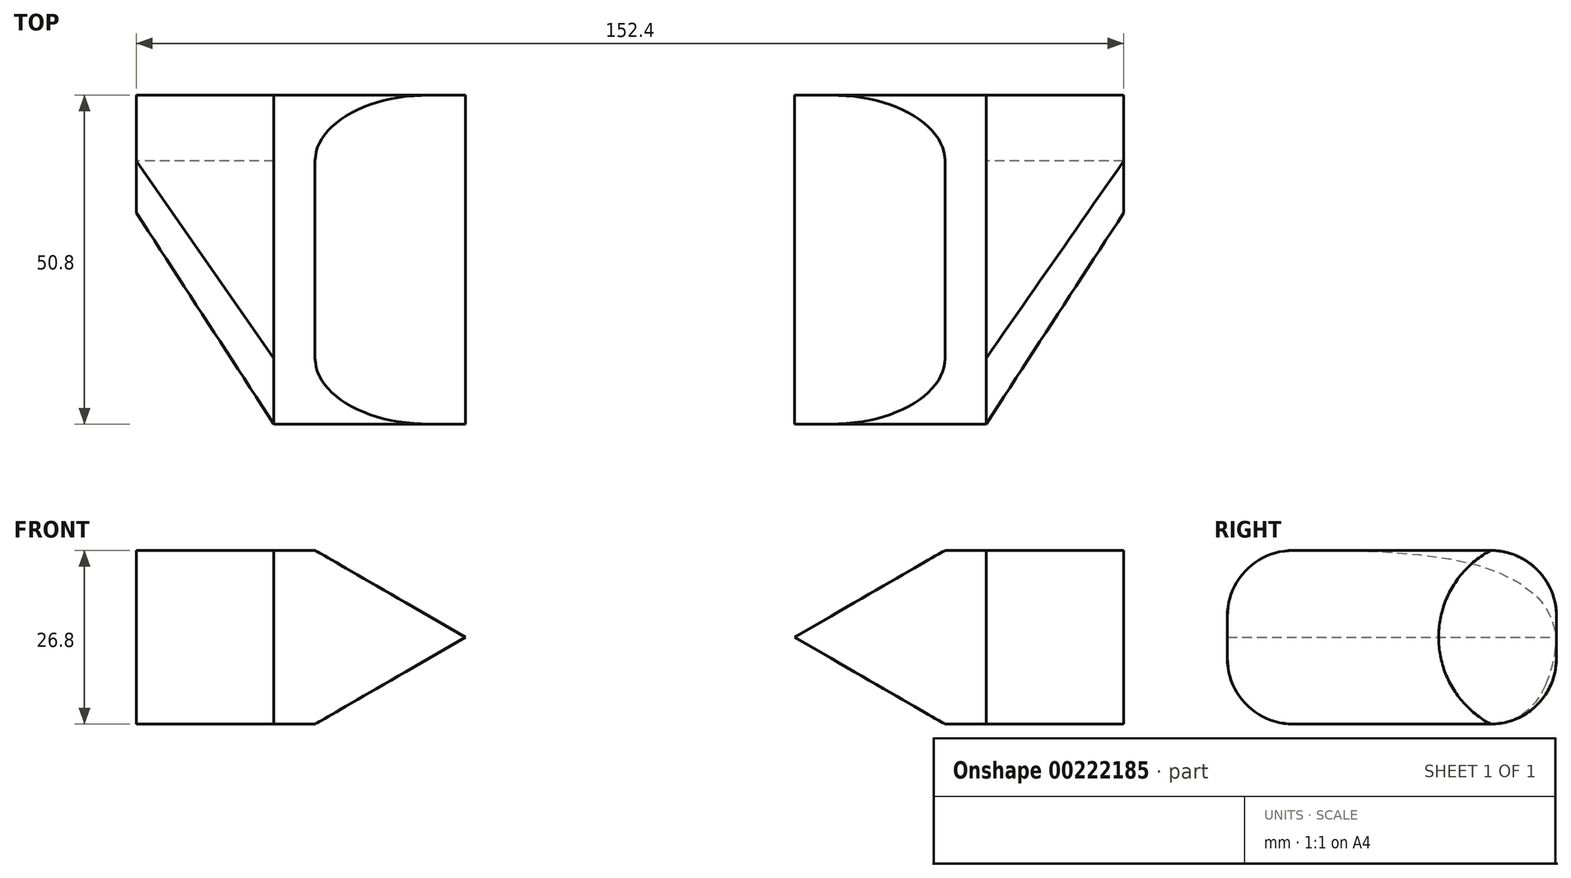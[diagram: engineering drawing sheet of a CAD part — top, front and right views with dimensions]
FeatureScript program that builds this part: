
annotation { "Feature Type Name" : "Feature", "Feature Type Description" : "" }
export const myFeature = defineFeature(function(context is Context, id is Id, definition is map)
    precondition{}
    {
        {
            var Q0;
            Q0=qCreatedBy(makeId("Front.planeOp"),FACE);
            var sketch = newSketch(context, id + "F0", { "sketchPlane" : qUnion([Q0])});
            skLineSegment(sketch, "E0", {"start": v(0, 47.56) * mm, "end": v(0, -56.2) * mm, "construction": true});
            skLineSegment(sketch, "E1", {"start": v(0, 0) * mm, "end": v(25.4, 0) * mm, "construction": true});
            skLineSegment(sketch, "E2.MirrorCS", {"start": v(0, 0) * mm, "end": v(-25.4, 0) * mm, "construction": true});
            skLineSegment(sketch, "E3", {"start": v(-25.4, 0) * mm, "end": v(-48.62, -13.4) * mm});
            skLineSegment(sketch, "E4", {"start": v(-48.62, -13.4) * mm, "end": v(-48.62, 13.4) * mm});
            skLineSegment(sketch, "E5", {"start": v(-48.62, 13.4) * mm, "end": v(-25.4, 0) * mm});
            skSolve(sketch);
        }
        {
            var Q0;
            Q0=makeQuery(id+"F0.imprint","IMPRINT",FACE,{"disambiguationData":[TD([[makeQuery(id+"F0.imprint","IMPRINT",EDGE,{"derivedFrom":sQuery(id+"F0.wireOp",EDGE,"E3")}),-1.0]])]});
            extrude(context, id + "F1", {"entities" : qUnion([Q0]), "depth" : 50.8 * mm});
        }
        {
            var Q0;
            Q0=makeQuery(id+"F1.opExtrude","SWEPT_FACE",FACE,{"disambiguationData":[OSD([sQuery(id+"F0.wireOp",EDGE,"E4")])]});
            extrude(context, id + "F2", {"entities" : qUnion([Q0]), "operationType" : NewBodyOperationType.ADD, "depth" : 6.35 * mm});
        }
        {
            var Q0;
            {var subQ0=sQuery(id+"F0.wireOp",EDGE,"E5");var subQ1=sQuery(id+"F0.wireOp",EDGE,"E4");Q0=makeQuery(id+"F2.opExtrude","SWEPT_EDGE",EDGE,{"disambiguationData":[OSD([subQ1,subQ0]),TDD([makeQuery(id+"F1.opExtrude","CAP_VERTEX",VERTEX,{"disambiguationData":[OSD([subQ1,subQ0])],"isStart":true})])]});}
            var Q1;
            {var subQ0=sQuery(id+"F0.wireOp",EDGE,"E4");var subQ1=sQuery(id+"F0.wireOp",EDGE,"E3");Q1=makeQuery(id+"F2.opExtrude","SWEPT_EDGE",EDGE,{"disambiguationData":[OSD([subQ1,subQ0]),TDD([makeQuery(id+"F1.opExtrude","CAP_VERTEX",VERTEX,{"disambiguationData":[OSD([subQ1,subQ0])],"isStart":true})])]});}
            var Q2;
            {var subQ0=sQuery(id+"F0.wireOp",EDGE,"E4");var subQ1=sQuery(id+"F0.wireOp",EDGE,"E3");Q2=makeQuery(id+"F2.opExtrude","SWEPT_EDGE",EDGE,{"disambiguationData":[OSD([subQ1,subQ0]),TDD([makeQuery(id+"F1.opExtrude","CAP_VERTEX",VERTEX,{"disambiguationData":[OSD([subQ1,subQ0])],"isStart":false})])]});}
            var Q3;
            {var subQ0=sQuery(id+"F0.wireOp",EDGE,"E5");var subQ1=sQuery(id+"F0.wireOp",EDGE,"E4");Q3=makeQuery(id+"F2.opExtrude","SWEPT_EDGE",EDGE,{"disambiguationData":[OSD([subQ1,subQ0]),TDD([makeQuery(id+"F1.opExtrude","CAP_VERTEX",VERTEX,{"disambiguationData":[OSD([subQ1,subQ0])],"isStart":false})])]});}
            fillet(context, id + "F3", {"entities" : qUnion([Q0, Q1, Q2, Q3]), "radius" : 10.16 * mm, "tangentPropagation" : true, "allowEdgeOverflow" : false});
        }
        {
            var Q0;
            Q0=qCreatedBy(makeId("Right.planeOp"),FACE);
            cPlane(context, id + "F4", {"entities" : qUnion([Q0]), "cplaneType" : CPlaneType.OFFSET, "offset" : 76.2 * mm, "oppositeDirection" : true, "width" : 152.4 * mm, "height" : 152.4 * mm});
        }
        {
            var Q0;
            Q0=qCreatedBy(id+"F4.planeOp",FACE);
            var sketch = newSketch(context, id + "F5", { "sketchPlane" : qUnion([Q0])});
            skLineSegment(sketch, "E6.0.0", {"start": v(0, 3.24) * mm, "end": v(0, -3.24) * mm});
            skArc(sketch, "E6.0.1", {"start": v(0, -3.24) * mm, "mid": v(-2.98, -10.43) * mm, "end": v(-10.16, -13.4) * mm});
            skLineSegment(sketch, "E6.0.4", {"start": v(-50.8, -3.24) * mm, "end": v(-50.8, 3.24) * mm});
            skArc(sketch, "E6.0.7", {"start": v(-10.16, 13.4) * mm, "mid": v(-2.98, 10.43) * mm, "end": v(0, 3.24) * mm});
            skArc(sketch, "E7", {"start": v(-10.16, 13.4) * mm, "mid": v(-18.19, 0) * mm, "end": v(-10.16, -13.4) * mm});
            skPoint(sketch, "E6.0.3.start.orphan", {"position": v(-40.64, -13.4) * mm});
            skPoint(sketch, "E6.0.6.start.orphan", {"position": v(-40.64, 13.4) * mm});
            skSolve(sketch);
        }
        {
            var Q1;
            Q1=makeQuery(id+"F2.opExtrude","CAP_FACE",FACE,{"disambiguationData":[OSD([sQuery(id+"F0.wireOp",EDGE,"E4")])],"isStart":false});
            var Q2;
            Q2=makeQuery(id+"F5.imprint","IMPRINT",FACE,{"disambiguationData":[TD([[makeQuery(id+"F5.imprint","IMPRINT",EDGE,{"derivedFrom":sQuery(id+"F5.wireOp",EDGE,"E6.0.0")}),-1.0]])]});
            loft(context, id + "F6", {"operationType" : NewBodyOperationType.ADD, "sheetProfilesArray" : [{ "sheetProfileEntities" : qUnion([Q1]) }, { "sheetProfileEntities" : qUnion([Q2]) }]});
        }
        {
            var Q0;
            Q0=makeQuery(id+"F1.opExtrude","SWEPT_BODY",BODY,{"disambiguationData":[OSD([sQuery(id+"F0.wireOp",EDGE,"E3"),sQuery(id+"F0.wireOp",EDGE,"E4"),sQuery(id+"F0.wireOp",EDGE,"E5")])]});
            var Q1;
            Q1=qCreatedBy(makeId("Right.planeOp"),FACE);
            mirror(context, id + "F7", {"entities" : qUnion([Q0]), "mirrorPlane" : qUnion([Q1])});
        }
    });
